# Revit family: Deckel_Anbau_Abzweigstück_Russia
name_source: partatom
category: Generic Models
revit_build: Autodesk Revit 2015 (Build: 20140606_1530(x64)
units: mm (PartAtom-declared; Revit-internal decimal feet)

## types (7) — shared parameters
Manufacturer = OBO Bettermann
Material = Steel, Galvanized
URL = http://www.obo-bettermann.com

## per-type parameters (varying)
| type | A | GTIN | L | Manufacturer Art. No. |
| DFAA 100 FS RU | 106 mm | 4012196606382 | 206 mm | 7128531 |
| DFAA 150 FS RU | 156 mm | 4012196649471 | 256 mm | 7128532 |
| DFAA 200 FS RU | 206 mm | 4012196606399 | 306 mm | 7128533 |
| DFAA 300 FS RU | 306 mm | 4012196606405 | 406 mm | 7128535 |
| DFAA 400 FS RU | 406 mm | 4012196626410 | 506 mm | 7128537 |
| DFAA 500 FS RU | 506 mm | 4012196626427 | 606 mm | 7128539 |
| DFAA 600 FS RU | 606 mm | 4012196626434 | 706 mm | 7128541 |

note: column(s) folded — value = type name in every type: Article Type

## geometry (parser evidence)
native form markers: Sweep x2
no freeform markers — native parametric forms only
